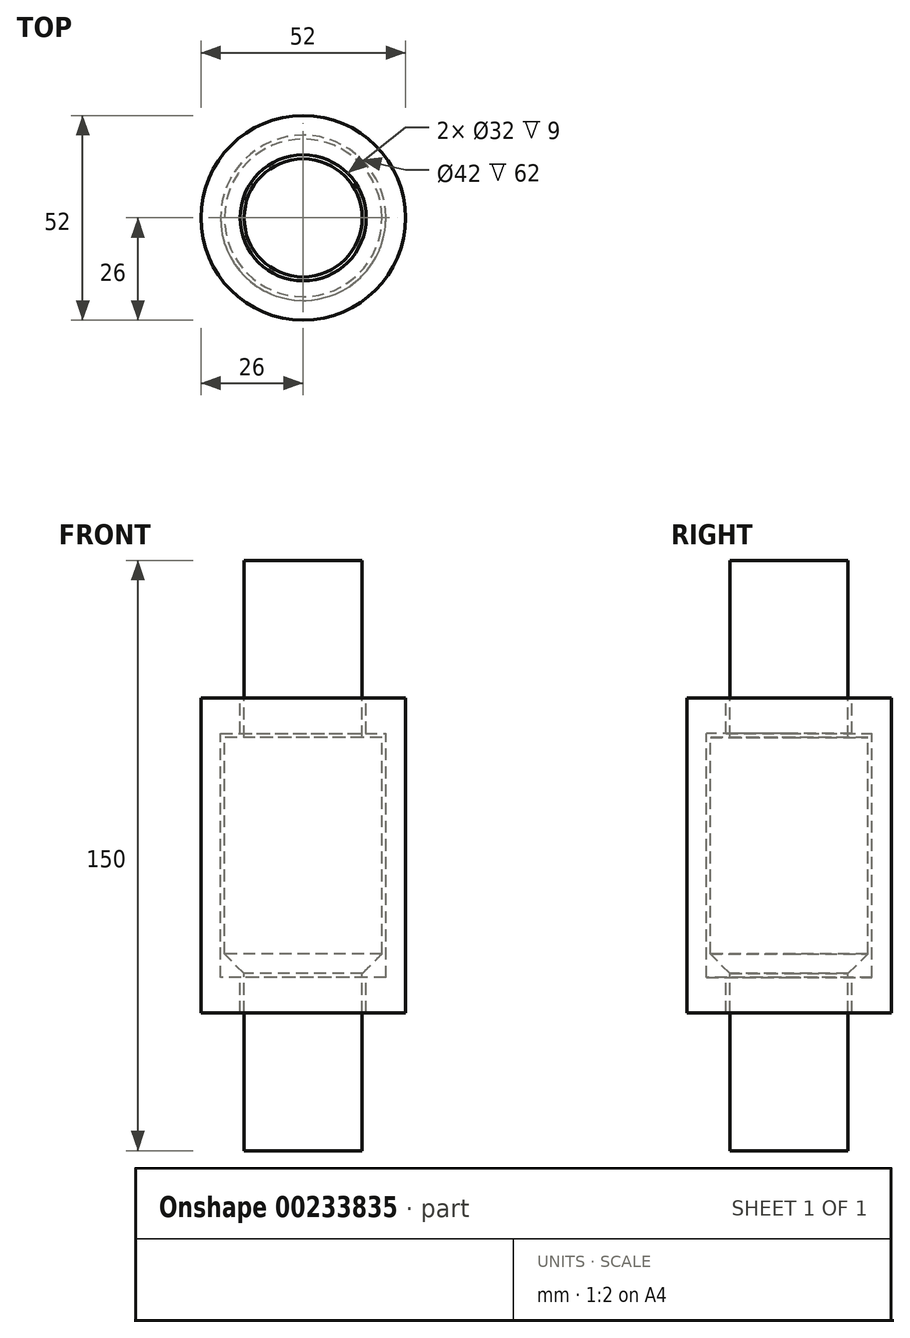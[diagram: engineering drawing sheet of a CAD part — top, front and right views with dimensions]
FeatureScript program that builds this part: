
annotation { "Feature Type Name" : "Feature", "Feature Type Description" : "" }
export const myFeature = defineFeature(function(context is Context, id is Id, definition is map)
    precondition{}
    {
        {
            var Q0;
            Q0=qCreatedBy(makeId("Front.planeOp"),FACE);
            var sketch = newSketch(context, id + "F0", { "sketchPlane" : qUnion([Q0])});
            skLineSegment(sketch, "E0", {"start": v(0, 0) * mm, "end": v(26, 0) * mm});
            skLineSegment(sketch, "E1", {"start": v(26, 0) * mm, "end": v(26, 80) * mm});
            skLineSegment(sketch, "E2", {"start": v(26, 80) * mm, "end": v(0, 80) * mm});
            skLineSegment(sketch, "E3", {"start": v(0, 80) * mm, "end": v(0, 0) * mm});
            skSolve(sketch);
        }
        {
            var Q0;
            Q0=qCreatedBy(makeId("Front.planeOp"),FACE);
            var sketch = newSketch(context, id + "F1", { "sketchPlane" : qUnion([Q0])});
            skLineSegment(sketch, "E4", {"start": v(0, 0) * mm, "end": v(15.4, 0) * mm});
            skLineSegment(sketch, "E5", {"start": v(15, 10) * mm, "end": v(20, 10) * mm});
            skLineSegment(sketch, "E6", {"start": v(20, 10) * mm, "end": v(20, 70) * mm});
            skLineSegment(sketch, "E7", {"start": v(20, 70) * mm, "end": v(15, 70) * mm});
            skLineSegment(sketch, "E8", {"start": v(0, 115) * mm, "end": v(0, -35) * mm});
            skLineSegment(sketch, "E9", {"start": v(0, 115) * mm, "end": v(15, 115) * mm});
            skLineSegment(sketch, "E10", {"start": v(15, 115) * mm, "end": v(15, 70) * mm});
            skLineSegment(sketch, "E11", {"start": v(15, -35) * mm, "end": v(0, -35) * mm});
            skPoint(sketch, "E12.0.end.orphan", {"position": v(0, 80) * mm});
            skLineSegment(sketch, "E13.trimOffspring", {"start": v(15, 10) * mm, "end": v(15, -35) * mm});
            skSolve(sketch);
        }
        {
            var Q0;
            Q0=qSketchRegion(id+"F0",true);
            var Q1;
            Q1=sQuery(id+"F1.wireOp",EDGE,"E8");
            revolve(context, id + "F2", {"entities" : qUnion([Q0]), "axis" : qUnion([Q1]), "revolveType" : RevolveType.FULL});
        }
        {
            var Q0;
            Q0=qSketchRegion(id+"F1",true);
            var Q1;
            Q1=sQuery(id+"F1.wireOp",EDGE,"E8");
            revolve(context, id + "F3", {"entities" : qUnion([Q0]), "axis" : qUnion([Q1]), "revolveType" : RevolveType.FULL});
        }
        {
            var Q0;
            Q0=makeQuery(id+"F3.opRevolve","SWEPT_BODY",BODY,{"disambiguationData":[OSD([sQuery(id+"F1.wireOp",EDGE,"E5"),sQuery(id+"F1.wireOp",EDGE,"E6"),sQuery(id+"F1.wireOp",EDGE,"E7"),sQuery(id+"F1.wireOp",EDGE,"E8"),sQuery(id+"F1.wireOp",EDGE,"E9"),sQuery(id+"F1.wireOp",EDGE,"E10"),sQuery(id+"F1.wireOp",EDGE,"E11"),sQuery(id+"F1.wireOp",EDGE,"E13.trimOffspring")])]});
            var Q1;
            Q1=makeQuery(id+"F2.opRevolve","SWEPT_BODY",BODY,{"disambiguationData":[OSD([sQuery(id+"F0.wireOp",EDGE,"E0"),sQuery(id+"F0.wireOp",EDGE,"E1"),sQuery(id+"F0.wireOp",EDGE,"E2"),sQuery(id+"F0.wireOp",EDGE,"E3")])]});
            booleanBodies(context, id + "F4", {"operationType" : BooleanOperationType.SUBTRACTION, "tools" : qUnion([Q0]), "targets" : qUnion([Q1]), "offset" : true, "offsetAll" : true, "offsetDistance" : 1 * mm, "keepTools" : true});
        }
        {
            var Q0;
            Q0=makeQuery(id+"F3.opRevolve","SWEPT_EDGE",EDGE,{"disambiguationData":[OSD([sQuery(id+"F1.wireOp",EDGE,"E5"),sQuery(id+"F1.wireOp",EDGE,"E6")])]});
            chamfer(context, id + "F5", {"entities" : qUnion([Q0]), "width" : 5 * mm, "tangentPropagation" : true});
        }
        {
            var Q0;
            Q0=makeQuery(id+"F3.opRevolve","SWEPT_FACE",FACE,{"disambiguationData":[OSD([sQuery(id+"F1.wireOp",EDGE,"E9")])]});
            var sketch = newSketch(context, id + "F6", { "sketchPlane" : qUnion([Q0])});
            skLineSegment(sketch, "E14", {"start": v(0, 0) * mm, "end": v(-15, 0) * mm});
            skLineSegment(sketch, "E15", {"start": v(0, 0) * mm, "end": v(15, 0) * mm});
            skLineSegment(sketch, "E16", {"start": v(-15, 0) * mm, "end": v(-35, 0) * mm});
            skLineSegment(sketch, "E17", {"start": v(-35, 0) * mm, "end": v(-35, -130) * mm});
            skLineSegment(sketch, "E18", {"start": v(-35, -130) * mm, "end": v(35, -130) * mm});
            skLineSegment(sketch, "E19", {"start": v(35, -130) * mm, "end": v(35, 0) * mm});
            skLineSegment(sketch, "E20", {"start": v(35, 0) * mm, "end": v(0, 0) * mm});
            skLineSegment(sketch, "E21", {"start": v(28.43, 0) * mm, "end": v(35, -125.14) * mm});
            skLineSegment(sketch, "E22", {"start": v(-28.43, 0) * mm, "end": v(-35, -125.14) * mm});
            skLineSegment(sketch, "E23", {"start": v(0, 0) * mm, "end": v(0, -116.48) * mm, "construction": true});
            skLineSegment(sketch, "E24.bottom", {"start": v(-10, -130) * mm, "end": v(10, -130) * mm});
            skLineSegment(sketch, "E24.top", {"start": v(-10, -120) * mm, "end": v(10, -120) * mm});
            skLineSegment(sketch, "E24.left", {"start": v(-10, -130) * mm, "end": v(-10, -120) * mm});
            skLineSegment(sketch, "E24.right", {"start": v(10, -130) * mm, "end": v(10, -120) * mm});
            skSolve(sketch);
        }
        {
            var Q0;
            {var subQ0=sQuery(id+"F6.wireOp",EDGE,"E18");Q0=makeQuery(id+"F6.imprint","IMPRINT",FACE,{"disambiguationData":[TD([[makeQuery(id+"F6.imprint","IMPRINT",EDGE,{"derivedFrom":subQ0}),1.0]])]});}
            var Q1;
            {var subQ0=sQuery(id+"F6.wireOp",EDGE,"E14");Q1=makeQuery(id+"F6.imprint","IMPRINT",FACE,{"disambiguationData":[TD([[makeQuery(id+"F6.imprint","IMPRINT",EDGE,{"derivedFrom":subQ0}),1.0]])]});}
            extrude(context, id + "F7", {"entities" : qUnion([Q0, Q1]), "oppositeDirection" : true, "depth" : 25 * mm});
        }
        {
            var Q0;
            Q0=makeQuery(id+"F3.opRevolve","SWEPT_BODY",BODY,{"disambiguationData":[OSD([sQuery(id+"F1.wireOp",EDGE,"E5"),sQuery(id+"F1.wireOp",EDGE,"E6"),sQuery(id+"F1.wireOp",EDGE,"E7"),sQuery(id+"F1.wireOp",EDGE,"E8"),sQuery(id+"F1.wireOp",EDGE,"E9"),sQuery(id+"F1.wireOp",EDGE,"E10"),sQuery(id+"F1.wireOp",EDGE,"E11"),sQuery(id+"F1.wireOp",EDGE,"E13.trimOffspring")])]});
            var Q1;
            Q1=makeQuery(id+"F7.opExtrude","SWEPT_BODY",BODY,{"disambiguationData":[OSD([sQuery(id+"F6.wireOp",EDGE,"E14"),sQuery(id+"F6.wireOp",EDGE,"E16"),sQuery(id+"F6.wireOp",EDGE,"E17"),sQuery(id+"F6.wireOp",EDGE,"E18"),sQuery(id+"F6.wireOp",EDGE,"E19"),sQuery(id+"F6.wireOp",EDGE,"E20"),sQuery(id+"F6.wireOp",EDGE,"E21"),sQuery(id+"F6.wireOp",EDGE,"E22")])]});
            booleanBodies(context, id + "F8", {"operationType" : BooleanOperationType.SUBTRACTION, "tools" : qUnion([Q0]), "targets" : qUnion([Q1]), "offset" : true, "offsetAll" : true, "offsetDistance" : .5 * mm, "keepTools" : true});
        }
        {
            var Q0;
            Q0=makeQuery(id+"F7.opExtrude","SWEPT_BODY",BODY,{"disambiguationData":[OSD([sQuery(id+"F6.wireOp",EDGE,"E14"),sQuery(id+"F6.wireOp",EDGE,"E16"),sQuery(id+"F6.wireOp",EDGE,"E17"),sQuery(id+"F6.wireOp",EDGE,"E18"),sQuery(id+"F6.wireOp",EDGE,"E19"),sQuery(id+"F6.wireOp",EDGE,"E20"),sQuery(id+"F6.wireOp",EDGE,"E21"),sQuery(id+"F6.wireOp",EDGE,"E22"),sQuery(id+"F6.wireOp",EDGE,"E24.top"),sQuery(id+"F6.wireOp",EDGE,"E24.left"),sQuery(id+"F6.wireOp",EDGE,"E24.right")])]});
            deleteBodies(context, id + "F9", {"entities" : qUnion([Q0])});
        }
    });
